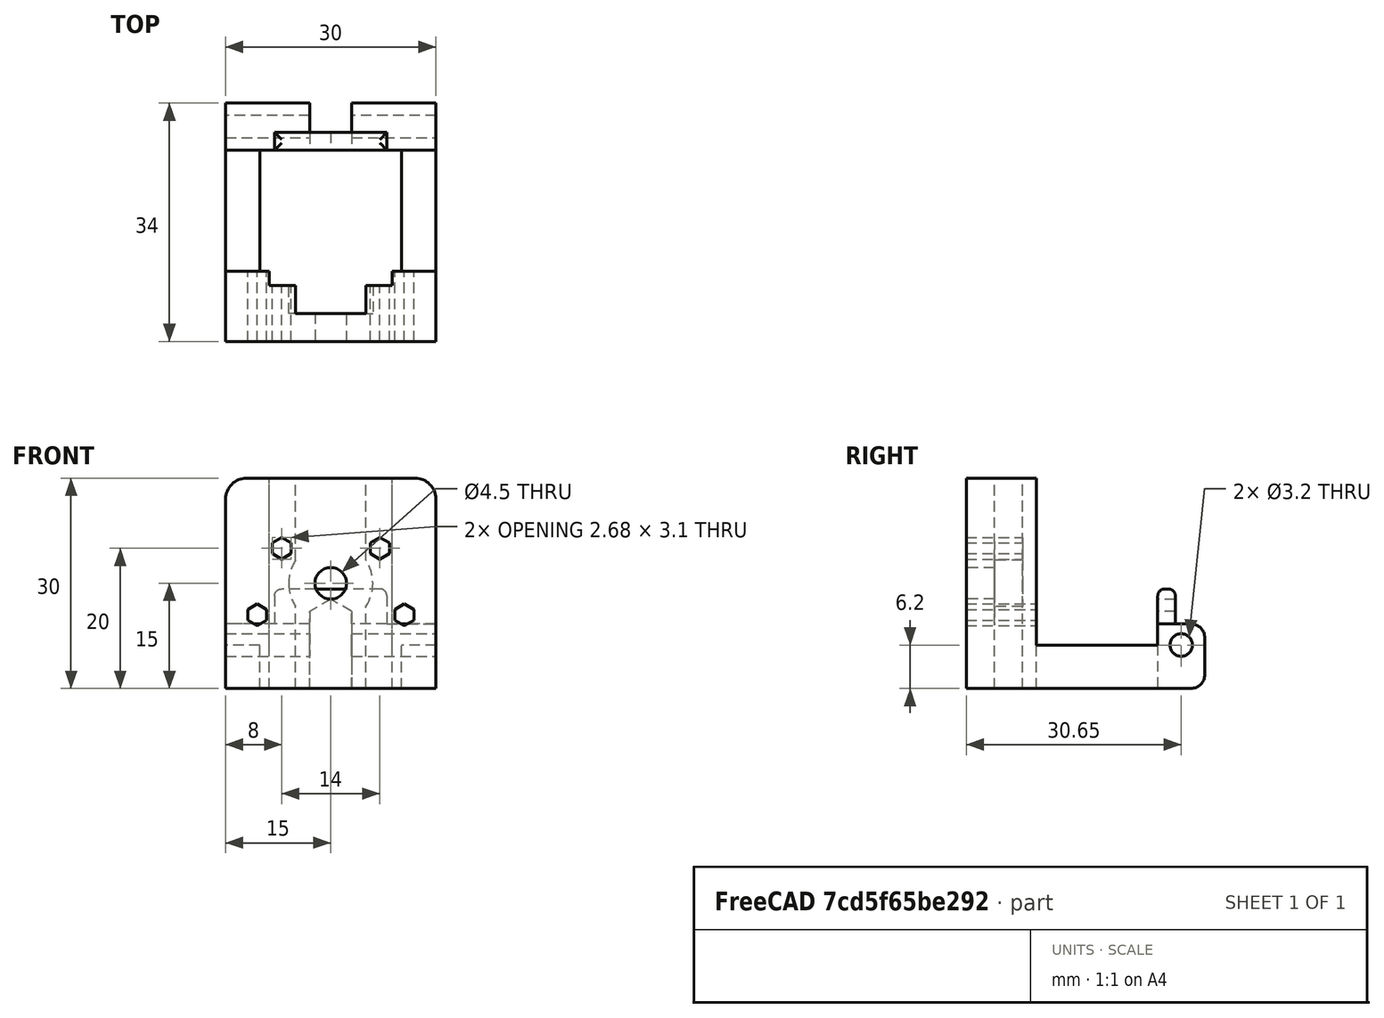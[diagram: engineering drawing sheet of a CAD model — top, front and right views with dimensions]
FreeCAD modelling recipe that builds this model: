
FCSTD DOCUMENT  (FreeCAD 0.19R24291 (Git))
Label: OptoEndStopCase_v5
License: All rights reserved
LicenseURL: http://en.wikipedia.org/wiki/All_rights_reserved
objects: Sketcher::SketchObject×5, PartDesign::Pocket×4, PartDesign::Fillet×3, PartDesign::Pad×1, PartDesign::Body×1, Mesh::Feature×1
note: 22 computed .brp shape members not serialized (recipe doc carries the construction recipe); baked Part::Feature solids carry a one-line shape summary decoded from their .brp

FEATURE [Sketcher::SketchObject] Sketch
  FullyConstrained = true
  MapMode = 5
  Support = -> [XY_Plane]
  sketch-geometry (16):
    g0: LineSegment StartX=15 StartY=34 StartZ=0 EndX=15 EndY=0 EndZ=0
    g1: LineSegment StartX=15 StartY=0 StartZ=0 EndX=-15 EndY=0 EndZ=0
    g2: LineSegment StartX=-15 StartY=0 StartZ=0 EndX=-15 EndY=34 EndZ=0
    g3: LineSegment StartX=10.1 StartY=27.3 StartZ=0 EndX=10.1 EndY=10 EndZ=0
    g4: LineSegment StartX=-10.1 StartY=10 StartZ=0 EndX=-10.1 EndY=27.3 EndZ=0
    g5: LineSegment StartX=-15 StartY=34 StartZ=0 EndX=15 EndY=34 EndZ=0
    g6: LineSegment StartX=10.1 StartY=27.3 StartZ=0 EndX=-10.1 EndY=27.3 EndZ=0
    g7: LineSegment StartX=-10.1 StartY=10 StartZ=0 EndX=-8.75 EndY=10 EndZ=0
    g8: LineSegment StartX=-8.75 StartY=10 StartZ=0 EndX=-8.75 EndY=8 EndZ=0
    g9: LineSegment StartX=-5 StartY=4 StartZ=0 EndX=5 EndY=4 EndZ=0
    g10: LineSegment StartX=8.75 StartY=8 StartZ=0 EndX=8.75 EndY=10 EndZ=0
    g11: LineSegment StartX=8.75 StartY=10 StartZ=0 EndX=10.1 EndY=10 EndZ=0
    g12: LineSegment StartX=5 StartY=4 StartZ=0 EndX=5 EndY=8 EndZ=0
    g13: LineSegment StartX=5 StartY=8 StartZ=0 EndX=8.75 EndY=8 EndZ=0
    g14: LineSegment StartX=-8.75 StartY=8 StartZ=0 EndX=-5 EndY=8 EndZ=0
    g15: LineSegment StartX=-5 StartY=8 StartZ=0 EndX=-5 EndY=4 EndZ=0
  constraints (46):
    c: Coincident(g0,g1)
    c: Coincident(g1,g2)
    c: Horizontal(g1)
    c: Vertical(g0)
    c: Vertical(g2)
    c: Vertical(g3)
    c: Vertical(g4)
    c: Distance(g3) = 17.3  'SensHeight'
    c: Coincident(g5,g2)
    c: Coincident(g6,g4)
    c: Distance(g1) = 30
    c: Coincident(g7,g4)
    c: Horizontal(g7)
    c: Coincident(g8,g7)
    c: Vertical(g8)
    c: Vertical(g10)
    c: Coincident(g11,g10)
    c: Coincident(g11,g3)
    c: Horizontal(g11)
    c: Distance(g4,g3) = 20.2
    c: Distance(g7,g10) = 17.5
    c: Equal(g10,g8)
    c: Symmetric(g4,g3,g-2)
    c: Coincident(g5,g0)
    c: Coincident(g6,g3)
    c: Distance(g2) = 34
    c: Symmetric(g0,g2,g-2)
    c: PointOnObject(g1,g-1)
    c: Coincident(g12,g9)
    c: Vertical(g12)
    c: Coincident(g13,g12)
    c: Coincident(g13,g10)
    c: Horizontal(g13)
    c: Coincident(g14,g8)
    c: Horizontal(g14)
    c: Coincident(g15,g14)
    c: Coincident(g15,g9)
    c: Vertical(g15)
    c: Distance(g9) = 10
    c: Symmetric(g9,g9,g-2)
    c: Equal(g3,g4)
    c: Distance(g8) = 2
    c: Distance(g9,g1) = 4
    c: Distance(g3,g5) = 6.7
    c: Equal(g11,g7)
    c: Distance(g7,g1) = 10  'BaseThin'
FEATURE [PartDesign::Pad] Pad
  Direction = (1,1,1)
  Length = 30
  Length2 = 100
  Midplane = true
  Profile = -> Sketch
  Type = 0
FEATURE [Sketcher::SketchObject] Sketch001
  ExternalGeometry = -> [Pad]
  FullyConstrained = false
  MapMode = 5
  Placement = pos=(0,0,0) rot=(0.57735,0.57735,0.57735;2.0944rad)
  Support = -> [YZ_Plane]
  expr: Constraints[29] = <<Sketch>>.Constraints.SensHeight
  expr: Constraints[32] = <<Sketch>>.Constraints.BaseThin
  sketch-geometry (12):
    g0: LineSegment StartX=10 StartY=15 StartZ=0 EndX=10 EndY=-8.8 EndZ=0
    g1: LineSegment StartX=10 StartY=-8.8 StartZ=0 EndX=27.3 EndY=-8.8 EndZ=0
    g2: LineSegment StartX=27.3 StartY=-8.8 StartZ=0 EndX=27.3 EndY=-0.8 EndZ=0
    g3: LineSegment StartX=27.3 StartY=-0.8 StartZ=0 EndX=29.8 EndY=-0.8 EndZ=0
    g4: LineSegment StartX=29.8 StartY=-0.8 StartZ=0 EndX=29.8 EndY=-5.8 EndZ=0
    g5: LineSegment StartX=34 StartY=-5.8 StartZ=0 EndX=29.8 EndY=-5.8 EndZ=0
    g6: LineSegment StartX=10 StartY=15 StartZ=0 EndX=34 EndY=15 EndZ=0
    g7: LineSegment StartX=34 StartY=15 StartZ=0 EndX=34 EndY=-5.8 EndZ=0
    g8: Circle CenterX=30.65 CenterY=-8.8 CenterZ=0 NormalX=0 NormalY=0 NormalZ=1 AngleXU=0 Radius=1.6
    g9: LineSegment StartX=38.9806 StartY=-8.8 StartZ=0 EndX=-1.45874 EndY=-8.8 EndZ=0
    g10: LineSegment StartX=27.3 StartY=16.0032 StartZ=0 EndX=27.3 EndY=-20.9006 EndZ=0
    g11: LineSegment StartX=10 StartY=20.1814 StartZ=0 EndX=10 EndY=-18.9366 EndZ=0
  constraints (33):
    c: PointOnObject(g0,g-3)
    c: Vertical(g0)
    c: Coincident(g1,g0)
    c: Horizontal(g1)
    c: Coincident(g2,g1)
    c: Vertical(g2)
    c: Coincident(g3,g2)
    c: Horizontal(g3)
    c: Vertical(g4)
    c: Coincident(g5,g4)
    c: Horizontal(g5)
    c: Coincident(g6,g0)
    c: Coincident(g6,g-4)
    c: Coincident(g7,g6)
    c: Coincident(g7,g5)
    c: Coincident(g3,g4)
    c: Horizontal(g9)
    c: Distance(g9,g-5) = 6.2
    c: PointOnObject(g1,g9)
    c: Distance(g4) = 5
    c: Diameter(g8) = 3.2
    c: Distance(g3) = 2.5
    c: Distance(g5,g9) = 3
    c: PointOnObject(g8,g9)
    c: Distance(g8,g2) = 3.35
    c: Distance(g8,g-4) = 3.35
    c: PointOnObject(g5,g-4)
    c: Vertical(g10)
    c: PointOnObject(g2,g10)
    c: Distance(g10,g0) = 17.3
    c: Vertical(g11)
    c: PointOnObject(g0,g11)
    c: Distance(g11,g-2) = 10
FEATURE [PartDesign::Pocket] Pocket
  BaseFeature = -> Pad
  Length = 5
  Length2 = 100
  Midplane = true
  Profile = -> Sketch001
  Type = 1
FEATURE [Sketcher::SketchObject] Sketch002
  ExternalGeometry = -> [Pocket]
  FullyConstrained = true
  MapMode = 5
  Placement = pos=(0,0,0) rot=(1,0,0;1.5708rad)
  Support = -> [Pocket]
  sketch-geometry (31):
    g0: Circle CenterX=0 CenterY=0 CenterZ=0 NormalX=0 NormalY=0 NormalZ=1 AngleXU=0 Radius=2.25
    g1: Circle CenterX=-7 CenterY=5 CenterZ=0 NormalX=0 NormalY=0 NormalZ=1 AngleXU=0 Radius=1.55
    g2: Circle CenterX=7 CenterY=5 CenterZ=0 NormalX=0 NormalY=0 NormalZ=1 AngleXU=0 Radius=1.55
    g3: LineSegment StartX=-5.65766 StartY=4.225 StartZ=0 EndX=-5.65766 EndY=5.775 EndZ=0
    g4: LineSegment StartX=-5.65766 StartY=5.775 StartZ=0 EndX=-7 EndY=6.55 EndZ=0
    g5: LineSegment StartX=-7 StartY=6.55 StartZ=0 EndX=-8.34234 EndY=5.775 EndZ=0
    g6: LineSegment StartX=-8.34234 StartY=5.775 StartZ=0 EndX=-8.34234 EndY=4.225 EndZ=0
    g7: LineSegment StartX=-8.34234 StartY=4.225 StartZ=0 EndX=-7 EndY=3.45 EndZ=0
    g8: LineSegment StartX=-7 StartY=3.45 StartZ=0 EndX=-5.65766 EndY=4.225 EndZ=0
    g9: Circle CenterX=-7 CenterY=5 CenterZ=0 NormalX=0 NormalY=0 NormalZ=1 AngleXU=0 Radius=1.55
    g10: LineSegment StartX=7 StartY=3.45 StartZ=0 EndX=8.34234 EndY=4.225 EndZ=0
    g11: LineSegment StartX=8.34234 StartY=4.225 StartZ=0 EndX=8.34234 EndY=5.775 EndZ=0
    g12: LineSegment StartX=8.34234 StartY=5.775 StartZ=0 EndX=7 EndY=6.55 EndZ=0
    g13: LineSegment StartX=7 StartY=6.55 StartZ=0 EndX=5.65766 EndY=5.775 EndZ=0
    g14: LineSegment StartX=5.65766 StartY=5.775 StartZ=0 EndX=5.65766 EndY=4.225 EndZ=0
    g15: LineSegment StartX=5.65766 StartY=4.225 StartZ=0 EndX=7 EndY=3.45 EndZ=0
    g16: Circle CenterX=7 CenterY=5 CenterZ=0 NormalX=0 NormalY=0 NormalZ=1 AngleXU=0 Radius=1.55
    g17: LineSegment StartX=-9.15766 StartY=-3.725 StartZ=0 EndX=-10.5 EndY=-2.95 EndZ=0
    g18: LineSegment StartX=-10.5 StartY=-2.95 StartZ=0 EndX=-11.8423 EndY=-3.725 EndZ=0
    g19: LineSegment StartX=-11.8423 StartY=-3.725 StartZ=0 EndX=-11.8423 EndY=-5.275 EndZ=0
    g20: LineSegment StartX=-11.8423 StartY=-5.275 StartZ=0 EndX=-10.5 EndY=-6.05 EndZ=0
    g21: LineSegment StartX=-10.5 StartY=-6.05 StartZ=0 EndX=-9.15766 EndY=-5.275 EndZ=0
    g22: LineSegment StartX=-9.15766 StartY=-5.275 StartZ=0 EndX=-9.15766 EndY=-3.725 EndZ=0
    g23: Circle CenterX=-10.5 CenterY=-4.5 CenterZ=0 NormalX=0 NormalY=0 NormalZ=1 AngleXU=0 Radius=1.55
    g24: LineSegment StartX=10.5 StartY=-6.05 StartZ=0 EndX=11.8423 EndY=-5.275 EndZ=0
    g25: LineSegment StartX=11.8423 StartY=-5.275 StartZ=0 EndX=11.8423 EndY=-3.725 EndZ=0
    g26: LineSegment StartX=11.8423 StartY=-3.725 StartZ=0 EndX=10.5 EndY=-2.95 EndZ=0
    g27: LineSegment StartX=10.5 StartY=-2.95 StartZ=0 EndX=9.15766 EndY=-3.725 EndZ=0
    g28: LineSegment StartX=9.15766 StartY=-3.725 StartZ=0 EndX=9.15766 EndY=-5.275 EndZ=0
    g29: LineSegment StartX=9.15766 StartY=-5.275 StartZ=0 EndX=10.5 EndY=-6.05 EndZ=0
    g30: Circle CenterX=10.5 CenterY=-4.5 CenterZ=0 NormalX=0 NormalY=0 NormalZ=1 AngleXU=0 Radius=1.55
  constraints (72):
    c: PointOnObject(g0,g-2)
    c: Symmetric(g1,g2,g-2)
    c: Distance(g1,g2) = 14
    c: Equal(g2,g1)
    c: Diameter(g2) = 3.1
    c: Diameter(g0) = 4.5
    c: Distance(g2,g-3) = 20
    c: PointOnObject(g0,g-1)
    c: Coincident(g3,g4)
    c: Coincident(g4,g5)
    c: Coincident(g5,g6)
    c: Coincident(g6,g7)
    c: Coincident(g7,g8)
    c: Coincident(g8,g3)
    c: Equal(g3, g4-g8) x5
    c: PointOnObject(g3,g9)
    c: PointOnObject(g4,g9)
    c: PointOnObject(g5,g9)
    c: PointOnObject(g6,g9)
    c: PointOnObject(g7,g9)
    c: PointOnObject(g8,g9)
    c: Coincident(g9,g1)
    c: PointOnObject(g8,g1)
    c: Coincident(g10,g11)
    c: Coincident(g11,g12)
    c: Coincident(g12,g13)
    c: Coincident(g13,g14)
    c: Coincident(g14,g15)
    c: Coincident(g15,g10)
    c: Equal(g10, g11-g15) x5
    c: PointOnObject(g10,g16)
    c: PointOnObject(g11,g16)
    c: PointOnObject(g12,g16)
    c: PointOnObject(g13,g16)
    c: PointOnObject(g14,g16)
    c: PointOnObject(g15,g16)
    c: Coincident(g16,g2)
    c: Symmetric(g3,g13,g-2)
    c: Vertical(g3)
    c: Coincident(g17,g18)
    c: Coincident(g18,g19)
    c: Coincident(g19,g20)
    c: Coincident(g20,g21)
    c: Coincident(g21,g22)
    c: Coincident(g22,g17)
    c: Equal(g17, g18-g22) x5
    c: PointOnObject(g17,g23)
    c: PointOnObject(g18,g23)
    c: PointOnObject(g19,g23)
    c: PointOnObject(g20,g23)
    c: PointOnObject(g21,g23)
    c: PointOnObject(g22,g23)
    c: Coincident(g24,g25)
    c: Coincident(g25,g26)
    c: Coincident(g26,g27)
    c: Coincident(g27,g28)
    c: Coincident(g28,g29)
    c: Coincident(g29,g24)
    c: Equal(g24, g25-g29) x5
    c: PointOnObject(g24,g30)
    c: PointOnObject(g25,g30)
    c: PointOnObject(g26,g30)
    c: PointOnObject(g27,g30)
    c: PointOnObject(g28,g30)
    c: PointOnObject(g29,g30)
    c: Equal(g23,g30)
    c: Equal(g30,g1)
    c: Symmetric(g23,g30,g-2)
    c: Vertical(g22)
    c: Vertical(g28)
    c: Distance(g30,g-3) = 10.5
    c: Distance(g23,g30) = 21
FEATURE [PartDesign::Pocket] Pocket001
  BaseFeature = -> Pocket
  Length = 10
  Length2 = 100
  Profile = -> Sketch002
  Type = 0
FEATURE [Sketcher::SketchObject] Sketch005
  FullyConstrained = true
  MapMode = 5
  Placement = pos=(0,4,0) rot=(0,0.707107,0.707107;3.14159rad)
  Support = -> [Pocket001]
  sketch-geometry (1):
    g0: Circle CenterX=0 CenterY=0 CenterZ=0 NormalX=0 NormalY=0 NormalZ=1 AngleXU=0 Radius=6
  constraints (2):
    c: Coincident(g0,g-1)
    c: Diameter(g0) = 12
FEATURE [PartDesign::Pocket] Pocket004
  BaseFeature = -> Pocket001
  Length = 5
  Length2 = 100
  Profile = -> Sketch005
  Reversed = true
  Type = 0
FEATURE [Sketcher::SketchObject] Sketch006
  ExternalGeometry = -> [Pocket004]
  FullyConstrained = true
  MapMode = 5
  Placement = pos=(0,34,0) rot=(0,0.707107,0.707107;3.14159rad)
  Support = -> [Pocket004]
  sketch-geometry (13):
    g0: LineSegment StartX=-3 StartY=-15 StartZ=0 EndX=3 EndY=-15 EndZ=0
    g1: LineSegment StartX=3 StartY=-15 StartZ=0 EndX=3 EndY=-4 EndZ=0
    g2: LineSegment StartX=-3 StartY=-4 StartZ=0 EndX=-3 EndY=-15 EndZ=0
    g3: LineSegment StartX=-3 StartY=-4 StartZ=0 EndX=0 EndY=-2.26795 EndZ=0
    g4: LineSegment StartX=0 StartY=-2.26795 StartZ=0 EndX=3 EndY=-4 EndZ=0
    g5: LineSegment StartX=15 StartY=-0.8 StartZ=0 EndX=8 EndY=-0.8 EndZ=0
    g6: LineSegment StartX=8 StartY=-0.8 StartZ=0 EndX=8 EndY=-5.8 EndZ=0
    g7: LineSegment StartX=8 StartY=-5.8 StartZ=0 EndX=15 EndY=-5.8 EndZ=0
    g8: LineSegment StartX=15 StartY=-5.8 StartZ=0 EndX=15 EndY=-0.8 EndZ=0
    g9: LineSegment StartX=-15 StartY=-0.8 StartZ=0 EndX=-8 EndY=-0.8 EndZ=0
    g10: LineSegment StartX=-8 StartY=-0.8 StartZ=0 EndX=-8 EndY=-5.8 EndZ=0
    g11: LineSegment StartX=-8 StartY=-5.8 StartZ=0 EndX=-15 EndY=-5.8 EndZ=0
    g12: LineSegment StartX=-15 StartY=-5.8 StartZ=0 EndX=-15 EndY=-0.8 EndZ=0
  constraints (35):
    c: Coincident(g0,g1)
    c: Coincident(g2,g0)
    c: Horizontal(g0)
    c: Vertical(g1)
    c: Vertical(g2)
    c: PointOnObject(g0,g-3)
    c: Coincident(g3,g2)
    c: Coincident(g4,g3)
    c: Coincident(g4,g1)
    c: PointOnObject(g3,g-2)
    c: Symmetric(g2,g1,g-2)
    c: Angle(g3,g4) = 2.0944
    c: Distance(g1) = 11
    c: Distance(g0) = 6
    c: Coincident(g5,g6)
    c: Coincident(g6,g7)
    c: Coincident(g7,g8)
    c: Coincident(g8,g5)
    c: Horizontal(g5)
    c: Horizontal(g7)
    c: Vertical(g6)
    c: Vertical(g8)
    c: Coincident(g5,g-4)
    c: PointOnObject(g6,g-5)
    c: Coincident(g9,g10)
    c: Coincident(g10,g11)
    c: Coincident(g11,g12)
    c: Coincident(g12,g9)
    c: Horizontal(g11)
    c: Vertical(g10)
    c: Vertical(g12)
    c: Coincident(g9,g-4)
    c: PointOnObject(g10,g-5)
    c: Symmetric(g9,g5,g-2)
    c: Distance(g5) = 7
FEATURE [PartDesign::Pocket] Pocket005
  BaseFeature = -> Pocket004
  Length = 5
  Length2 = 100
  Profile = -> Sketch006
  Type = 2
FEATURE [PartDesign::Fillet] Fillet
  Base = -> Pocket005 [Edge11,Edge27,Edge85,Edge86,Edge141,Edge142]
  BaseFeature = -> Pocket005
  Radius = 2
  SupportTransform = false
FEATURE [PartDesign::Fillet] Fillet001
  Base = -> Fillet [Face83]
  BaseFeature = -> Fillet
  Radius = 1
  SupportTransform = false
FEATURE [PartDesign::Fillet] Fillet002
  Base = -> Fillet001 [Edge84,Edge73]
  BaseFeature = -> Fillet001
  Radius = 3
  SupportTransform = false
FEATURE [PartDesign::Body] Body
  Group = -> [Sketch,Pad,Sketch001,Pocket,Sketch002,Pocket001,Sketch005,Pocket004,Sketch006,Pocket005,Fillet,Fillet001,Fillet002]
  Origin = -> Origin
  Tip = -> Fillet002
FEATURE [Mesh::Feature] Mesh  label="Fillet002 (Meshed)"
